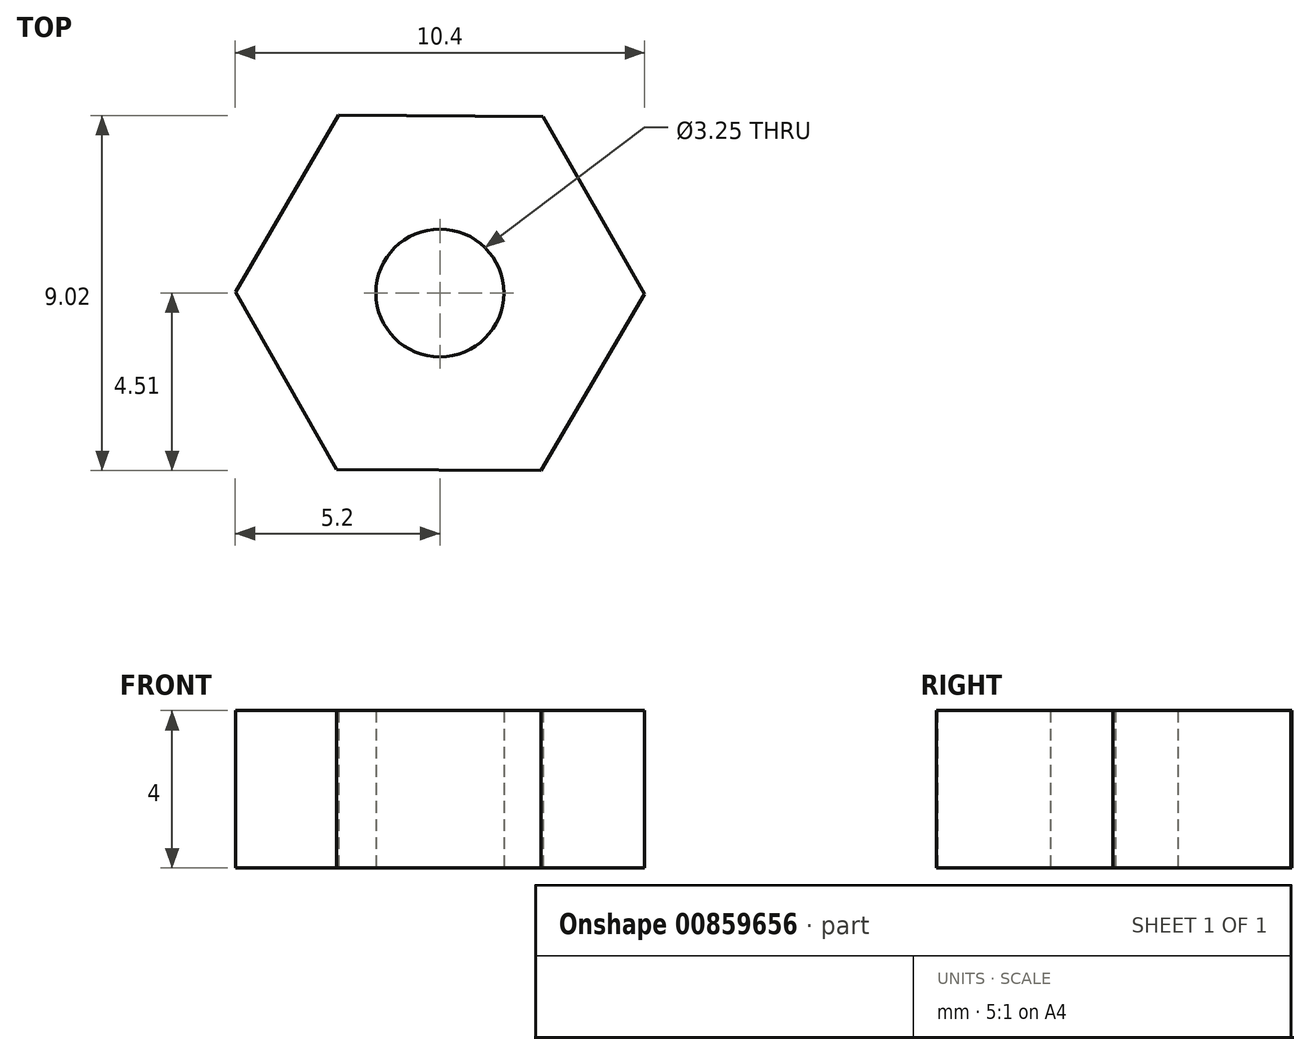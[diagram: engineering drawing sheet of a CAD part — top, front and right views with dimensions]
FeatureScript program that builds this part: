
annotation { "Feature Type Name" : "Feature", "Feature Type Description" : "" }
export const myFeature = defineFeature(function(context is Context, id is Id, definition is map)
    precondition{}
    {
        {
            var Q0;
            Q0=qCreatedBy(makeId("Top.planeOp"),FACE);
            var sketch = newSketch(context, id + "F0", { "sketchPlane" : qUnion([Q0])});
            skCircle(sketch, "E0", {"center": v(0, 0) * mm, "radius": 1.63 * mm});
            skCircle(sketch, "E1.cCircle", {"center": v(0, 0) * mm, "radius": 4.5 * mm, "construction": true});
            skLineSegment(sketch, "E1.0", {"start": v(5.2, -0.03) * mm, "end": v(2.57, -4.51) * mm});
            skLineSegment(sketch, "E1.1", {"start": v(2.57, -4.51) * mm, "end": v(-2.62, -4.49) * mm});
            skLineSegment(sketch, "E1.2", {"start": v(-2.62, -4.49) * mm, "end": v(-5.2, 0.03) * mm});
            skLineSegment(sketch, "E1.3", {"start": v(-5.2, 0.03) * mm, "end": v(-2.57, 4.51) * mm});
            skLineSegment(sketch, "E1.4", {"start": v(-2.57, 4.51) * mm, "end": v(2.62, 4.49) * mm});
            skLineSegment(sketch, "E1.5", {"start": v(2.62, 4.49) * mm, "end": v(5.2, -0.03) * mm});
            skPoint(sketch, "E1.0.midPoint", {"position": v(3.89, -2.27) * mm});
            skSolve(sketch);
        }
        {
            var Q0;
            Q0=makeQuery(id+"F0.imprint","IMPRINT",FACE,{"disambiguationData":[TD([[makeQuery(id+"F0.imprint","IMPRINT",EDGE,{"derivedFrom":sQuery(id+"F0.wireOp",EDGE,"E0")}),-1.0]])]});
            extrude(context, id + "F1", {"entities" : qUnion([Q0]), "depth" : 4 * mm, "offsetDistance" : 25 * mm});
        }
    });
